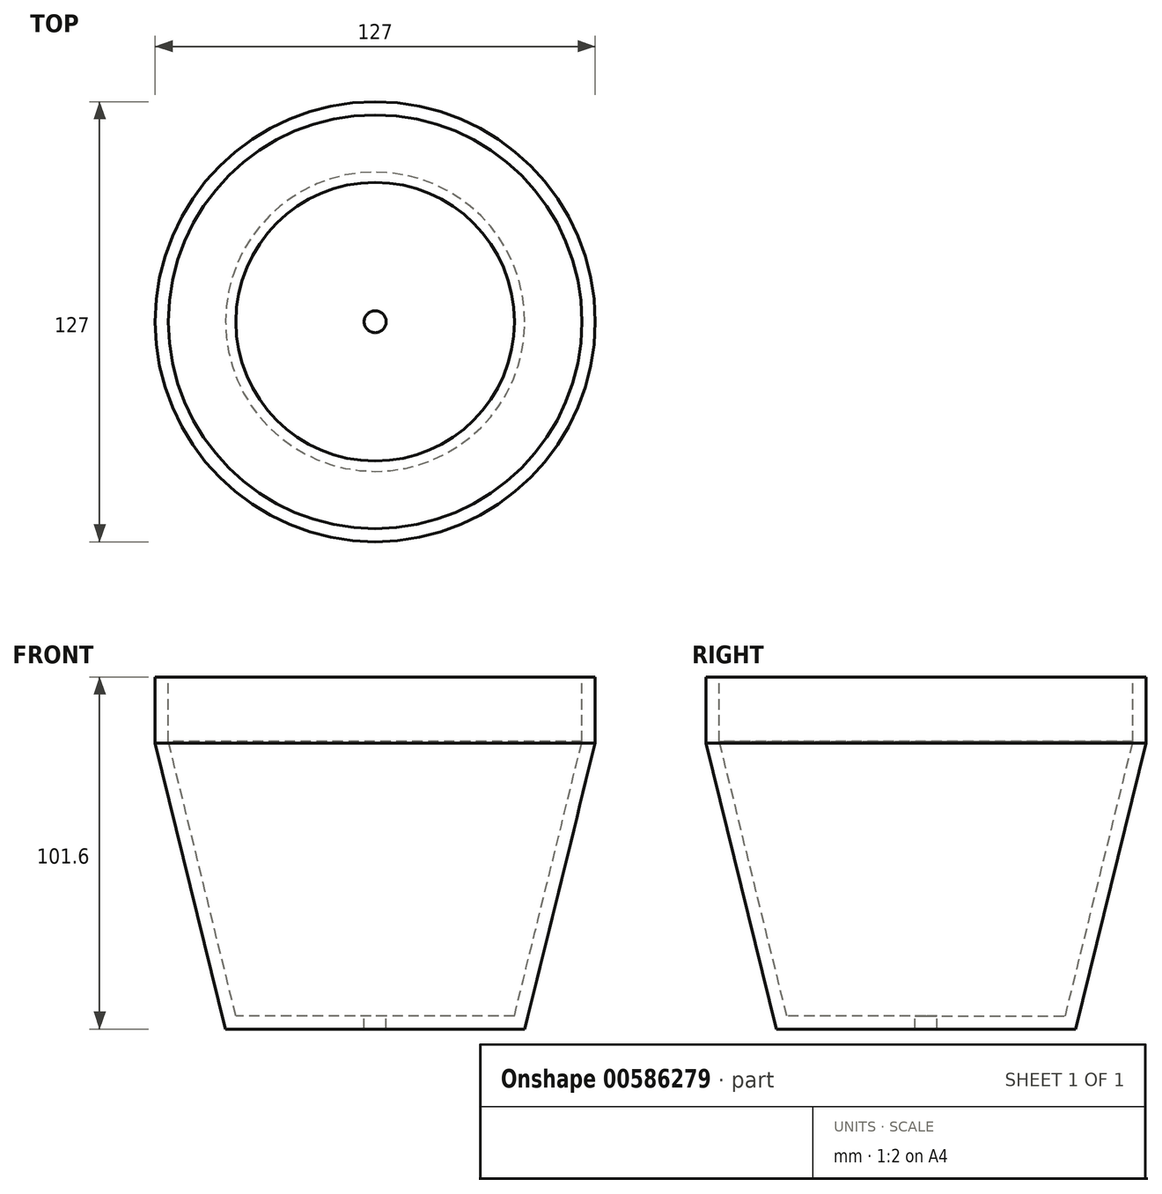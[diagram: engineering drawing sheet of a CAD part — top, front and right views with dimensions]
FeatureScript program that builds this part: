
annotation { "Feature Type Name" : "Feature", "Feature Type Description" : "" }
export const myFeature = defineFeature(function(context is Context, id is Id, definition is map)
    precondition{}
    {
        {
            var Q0;
            Q0=qCreatedBy(makeId("Front.planeOp"),FACE);
            var sketch = newSketch(context, id + "F0", { "sketchPlane" : qUnion([Q0])});
            skLineSegment(sketch, "E0", {"start": v(0, 132.66) * mm, "end": v(0, -118.93) * mm, "construction": true});
            skLineSegment(sketch, "E1", {"start": v(0, 56.4) * mm, "end": v(-63.5, 56.4) * mm});
            skLineSegment(sketch, "E2", {"start": v(-63.5, 56.4) * mm, "end": v(-63.5, 37.35) * mm});
            skLineSegment(sketch, "E3", {"start": v(-63.5, 37.35) * mm, "end": v(-43.18, -45.2) * mm});
            skLineSegment(sketch, "E4", {"start": v(-43.18, -45.2) * mm, "end": v(0, -45.2) * mm});
            skLineSegment(sketch, "E5", {"start": v(0, -45.2) * mm, "end": v(0, 56.4) * mm});
            skSolve(sketch);
        }
        {
            var Q0;
            Q0=qSketchRegion(id+"F0",true);
            var Q1;
            Q1=sQuery(id+"F0.wireOp",EDGE,"E0");
            revolve(context, id + "F1", {"entities" : qUnion([Q0]), "axis" : qUnion([Q1]), "revolveType" : RevolveType.FULL});
        }
        {
            var Q0;
            Q0=makeQuery(id+"F1.opRevolve","SWEPT_FACE",FACE,{"disambiguationData":[OSD([sQuery(id+"F0.wireOp",EDGE,"E1")])]});
            shell(context, id + "F2", {"entities" : qUnion([Q0]), "thickness" : 3.8 * mm});
        }
        {
            var Q0;
            Q0=makeQuery(id+"F2.opShell","OFFSET_FACE",FACE,{"disambiguationData":[OSD([sQuery(id+"F0.wireOp",EDGE,"E4")])]});
            var sketch = newSketch(context, id + "F3", { "sketchPlane" : qUnion([Q0])});
            skCircle(sketch, "E6", {"center": v(0, 0) * mm, "radius": 3.81 * mm});
            skSolve(sketch);
        }
        {
            var Q0;
            Q0=sQuery(id+"F3.wireOp",VERTEX,"E6.center");
            var Q1;
            Q1=makeQuery(id+"F1.opRevolve","SWEPT_BODY",BODY,{"disambiguationData":[OSD([sQuery(id+"F0.wireOp",EDGE,"E1"),sQuery(id+"F0.wireOp",EDGE,"E2"),sQuery(id+"F0.wireOp",EDGE,"6kxozgEL-SpZe-i6sA-ZBZo-EFmS46s4ymtp"),sQuery(id+"F0.wireOp",EDGE,"E3"),sQuery(id+"F0.wireOp",EDGE,"E4"),sQuery(id+"F0.wireOp",EDGE,"E5")])]});
            hole(context, id + "F4", {"style" : HoleStyle.SIMPLE, "endStyle" : HoleEndStyle.THROUGH, "holeDiameter" : 6.35 * mm, "isTappedThrough" : true, "tappedDepth" : 12.7 * mm, "tapClearance" : 3, "locations" : qUnion([Q0]), "scope" : qUnion([Q1])});
        }
    });
